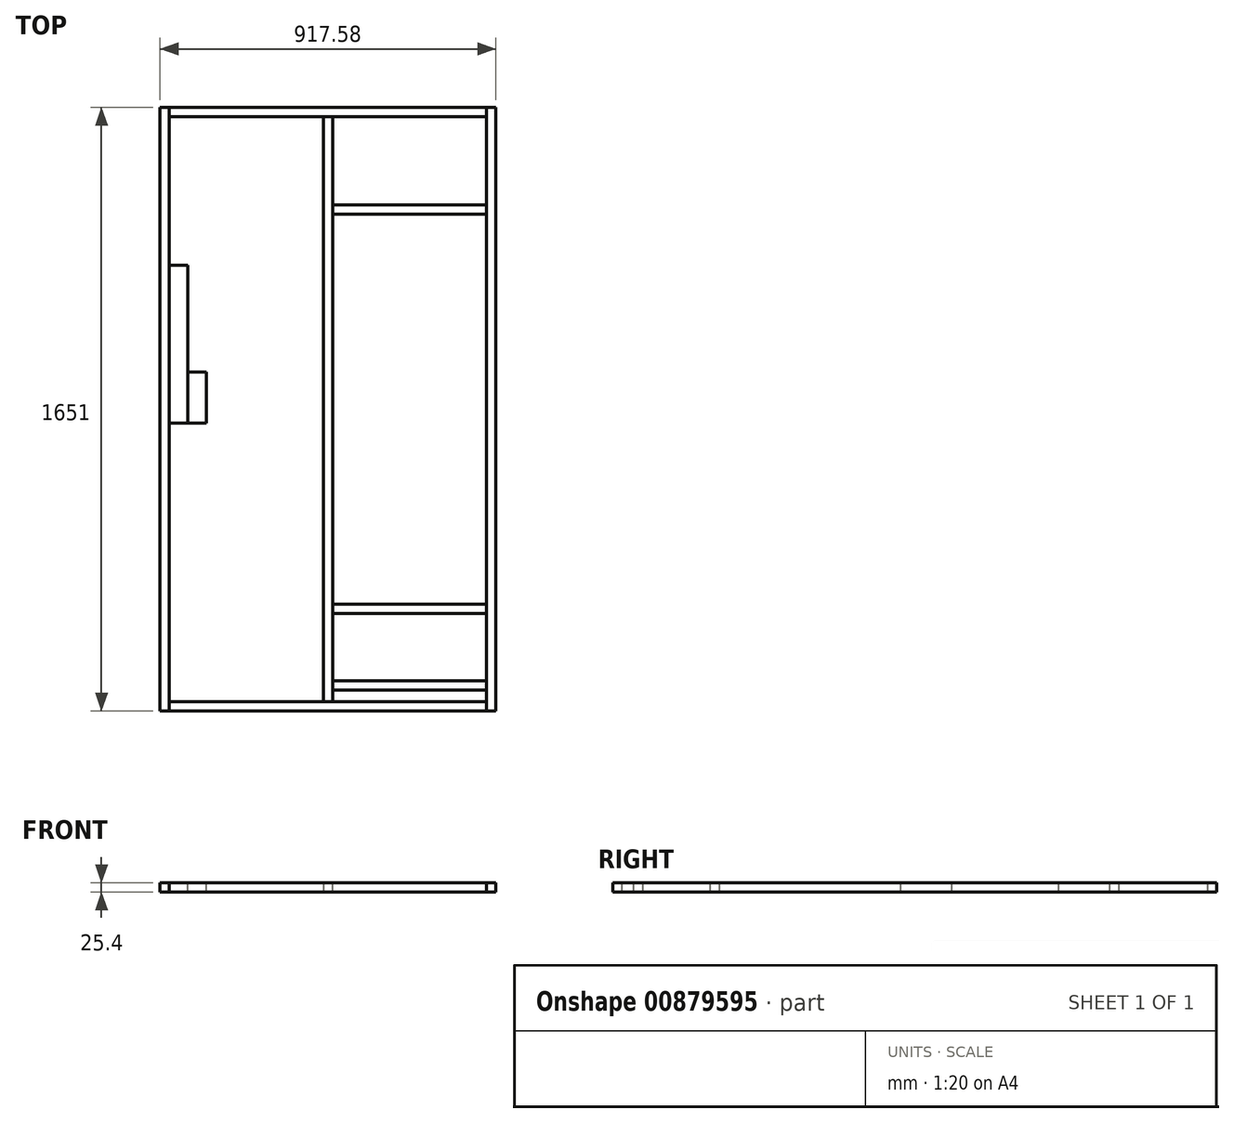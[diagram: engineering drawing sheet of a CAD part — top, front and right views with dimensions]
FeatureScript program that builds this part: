
annotation { "Feature Type Name" : "Feature", "Feature Type Description" : "" }
export const myFeature = defineFeature(function(context is Context, id is Id, definition is map)
    precondition{}
    {
        {
            var Q0;
            Q0=qCreatedBy(makeId("Top.planeOp"),FACE);
            var sketch = newSketch(context, id + "F0", { "sketchPlane" : qUnion([Q0])});
            skLineSegment(sketch, "E0.bottom", {"start": v(0, 0) * mm, "end": v(25.4, 0) * mm});
            skLineSegment(sketch, "E0.top", {"start": v(0, -1651) * mm, "end": v(25.4, -1651) * mm});
            skLineSegment(sketch, "E0.left", {"start": v(0, 0) * mm, "end": v(0, -1651) * mm});
            skLineSegment(sketch, "E0.right", {"start": v(25.4, 0) * mm, "end": v(25.4, -1651) * mm});
            skLineSegment(sketch, "E1.bottom", {"start": v(892.18, 0) * mm, "end": v(917.58, 0) * mm});
            skLineSegment(sketch, "E1.top", {"start": v(892.18, -1651) * mm, "end": v(917.58, -1651) * mm});
            skLineSegment(sketch, "E1.left", {"start": v(892.18, 0) * mm, "end": v(892.18, -1651) * mm});
            skLineSegment(sketch, "E1.right", {"start": v(917.58, 0) * mm, "end": v(917.58, -1651) * mm});
            skLineSegment(sketch, "E2", {"start": v(25.4, 0) * mm, "end": v(892.18, 0) * mm, "construction": true});
            skSolve(sketch);
        }
        {
            var Q0;
            Q0=qSketchRegion(id+"F0",true);
            extrude(context, id + "F1", {"entities" : qUnion([Q0]), "depth" : 25.4 * mm, "offsetDistance" : 25.4 * mm});
        }
        {
            var Q0;
            Q0=makeQuery(id+"F1.opExtrude","SWEPT_FACE",FACE,{"disambiguationData":[OSD([sQuery(id+"F0.wireOp",EDGE,"E0.right")])]});
            var sketch = newSketch(context, id + "F2", { "sketchPlane" : qUnion([Q0])});
            skLineSegment(sketch, "E3.bottom", {"start": v(0, 0) * mm, "end": v(-25.4, 0) * mm});
            skLineSegment(sketch, "E3.top", {"start": v(0, 25.4) * mm, "end": v(-25.4, 25.4) * mm});
            skLineSegment(sketch, "E3.left", {"start": v(0, 0) * mm, "end": v(0, 25.4) * mm});
            skLineSegment(sketch, "E3.right", {"start": v(-25.4, 0) * mm, "end": v(-25.4, 25.4) * mm});
            skLineSegment(sketch, "E4.bottom", {"start": v(-1651, 25.4) * mm, "end": v(-1625.6, 25.4) * mm});
            skLineSegment(sketch, "E4.top", {"start": v(-1651, 0) * mm, "end": v(-1625.6, 0) * mm});
            skLineSegment(sketch, "E4.left", {"start": v(-1651, 25.4) * mm, "end": v(-1651, 0) * mm});
            skLineSegment(sketch, "E4.right", {"start": v(-1625.6, 25.4) * mm, "end": v(-1625.6, 0) * mm});
            skSolve(sketch);
        }
        {
            var Q0;
            Q0=qSketchRegion(id+"F2",true);
            var Q1;
            Q1=makeQuery(id+"F1.opExtrude","SWEPT_FACE",FACE,{"disambiguationData":[OSD([sQuery(id+"F0.wireOp",EDGE,"E1.left")])]});
            extrude(context, id + "F3", {"entities" : qUnion([Q0]), "endBound" : BoundingType.UP_TO_SURFACE, "depth" : 25.4 * mm, "endBoundEntityFace" : qUnion([Q1]), "offsetDistance" : 25.4 * mm});
        }
        {
            var Q0;
            Q0=makeQuery(id+"F3.opExtrude","SWEPT_FACE",FACE,{"disambiguationData":[OSD([sQuery(id+"F2.wireOp",EDGE,"E4.right")])]});
            var sketch = newSketch(context, id + "F4", { "sketchPlane" : qUnion([Q0])});
            skLineSegment(sketch, "E5.bottom", {"start": v(-446.09, 0) * mm, "end": v(-471.49, 0) * mm});
            skLineSegment(sketch, "E5.top", {"start": v(-446.09, 25.4) * mm, "end": v(-471.49, 25.4) * mm});
            skLineSegment(sketch, "E5.left", {"start": v(-446.09, 0) * mm, "end": v(-446.09, 25.4) * mm});
            skLineSegment(sketch, "E5.right", {"start": v(-471.49, 0) * mm, "end": v(-471.49, 25.4) * mm});
            skLineSegment(sketch, "E6", {"start": v(-471.49, 12.7) * mm, "end": v(-892.18, 12.7) * mm, "construction": true});
            skLineSegment(sketch, "E7", {"start": v(-446.09, 12.7) * mm, "end": v(-25.4, 12.7) * mm, "construction": true});
            skSolve(sketch);
        }
        {
            var Q0;
            Q0=qSketchRegion(id+"F4",true);
            var Q1;
            Q1=makeQuery(id+"F3.opExtrude","SWEPT_FACE",FACE,{"disambiguationData":[OSD([sQuery(id+"F2.wireOp",EDGE,"E3.right")])]});
            extrude(context, id + "F5", {"entities" : qUnion([Q0]), "endBound" : BoundingType.UP_TO_SURFACE, "depth" : 25.4 * mm, "endBoundEntityFace" : qUnion([Q1]), "offsetDistance" : 25.4 * mm});
        }
        {
            var Q0;
            Q0=makeQuery(id+"F1.opExtrude","SWEPT_FACE",FACE,{"disambiguationData":[OSD([sQuery(id+"F0.wireOp",EDGE,"E1.left")])]});
            var sketch = newSketch(context, id + "F6", { "sketchPlane" : qUnion([Q0])});
            skLineSegment(sketch, "E8.bottom", {"start": v(266.7, 25.4) * mm, "end": v(292.1, 25.4) * mm});
            skLineSegment(sketch, "E8.top", {"start": v(266.7, 0) * mm, "end": v(292.1, 0) * mm});
            skLineSegment(sketch, "E8.left", {"start": v(266.7, 25.4) * mm, "end": v(266.7, 0) * mm});
            skLineSegment(sketch, "E8.right", {"start": v(292.1, 25.4) * mm, "end": v(292.1, 0) * mm});
            skLineSegment(sketch, "E9.bottom", {"start": v(1593.85, 25.4) * mm, "end": v(1568.45, 25.4) * mm});
            skLineSegment(sketch, "E9.top", {"start": v(1593.85, 0) * mm, "end": v(1568.45, 0) * mm});
            skLineSegment(sketch, "E9.left", {"start": v(1593.85, 25.4) * mm, "end": v(1593.85, 0) * mm});
            skLineSegment(sketch, "E9.right", {"start": v(1568.45, 25.4) * mm, "end": v(1568.45, 0) * mm});
            skLineSegment(sketch, "E10.bottom", {"start": v(1384.3, 25.4) * mm, "end": v(1358.9, 25.4) * mm});
            skLineSegment(sketch, "E10.top", {"start": v(1384.3, 0) * mm, "end": v(1358.9, 0) * mm});
            skLineSegment(sketch, "E10.left", {"start": v(1384.3, 25.4) * mm, "end": v(1384.3, 0) * mm});
            skLineSegment(sketch, "E10.right", {"start": v(1358.9, 25.4) * mm, "end": v(1358.9, 0) * mm});
            skSolve(sketch);
        }
        {
            var Q0;
            Q0=qSketchRegion(id+"F6",true);
            var Q1;
            Q1=makeQuery(id+"F5.opExtrude","SWEPT_FACE",FACE,{"disambiguationData":[OSD([sQuery(id+"F4.wireOp",EDGE,"E5.right")])]});
            extrude(context, id + "F7", {"entities" : qUnion([Q0]), "endBound" : BoundingType.UP_TO_SURFACE, "depth" : 25.4 * mm, "endBoundEntityFace" : qUnion([Q1]), "offsetDistance" : 25.4 * mm});
        }
        {
            var Q0;
            Q0=makeQuery(id+"F1.opExtrude","CAP_FACE",FACE,{"disambiguationData":[OSD([sQuery(id+"F0.wireOp",EDGE,"E0.bottom"),sQuery(id+"F0.wireOp",EDGE,"E0.top"),sQuery(id+"F0.wireOp",EDGE,"E0.left"),sQuery(id+"F0.wireOp",EDGE,"E0.right")])],"isStart":false});
            var sketch = newSketch(context, id + "F8", { "sketchPlane" : qUnion([Q0])});
            skLineSegment(sketch, "E11.bottom", {"start": v(25.4, -431.8) * mm, "end": v(76.2, -431.8) * mm});
            skLineSegment(sketch, "E11.top", {"start": v(25.4, -863.6) * mm, "end": v(76.2, -863.6) * mm});
            skLineSegment(sketch, "E11.left", {"start": v(25.4, -431.8) * mm, "end": v(25.4, -863.6) * mm});
            skLineSegment(sketch, "E11.right", {"start": v(76.2, -431.8) * mm, "end": v(76.2, -863.6) * mm});
            skSolve(sketch);
        }
        {
            var Q0;
            Q0=qSketchRegion(id+"F8",true);
            extrude(context, id + "F9", {"entities" : qUnion([Q0]), "oppositeDirection" : true, "depth" : 25.4 * mm, "offsetDistance" : 25.4 * mm});
        }
        {
            var Q0;
            Q0=makeQuery(id+"F9.opExtrude","CAP_FACE",FACE,{"disambiguationData":[OSD([sQuery(id+"F8.wireOp",EDGE,"E11.bottom"),sQuery(id+"F8.wireOp",EDGE,"E11.top"),sQuery(id+"F8.wireOp",EDGE,"E11.left"),sQuery(id+"F8.wireOp",EDGE,"E11.right")])],"isStart":true});
            var sketch = newSketch(context, id + "F10", { "sketchPlane" : qUnion([Q0])});
            skLineSegment(sketch, "E12.bottom", {"start": v(76.2, -863.6) * mm, "end": v(127, -863.6) * mm});
            skLineSegment(sketch, "E12.top", {"start": v(76.2, -723.9) * mm, "end": v(127, -723.9) * mm});
            skLineSegment(sketch, "E12.left", {"start": v(76.2, -863.6) * mm, "end": v(76.2, -723.9) * mm});
            skLineSegment(sketch, "E12.right", {"start": v(127, -863.6) * mm, "end": v(127, -723.9) * mm});
            skSolve(sketch);
        }
        {
            var Q0;
            Q0=qSketchRegion(id+"F10",true);
            extrude(context, id + "F11", {"entities" : qUnion([Q0]), "oppositeDirection" : true, "depth" : 25.4 * mm, "offsetDistance" : 25.4 * mm});
        }
    });
